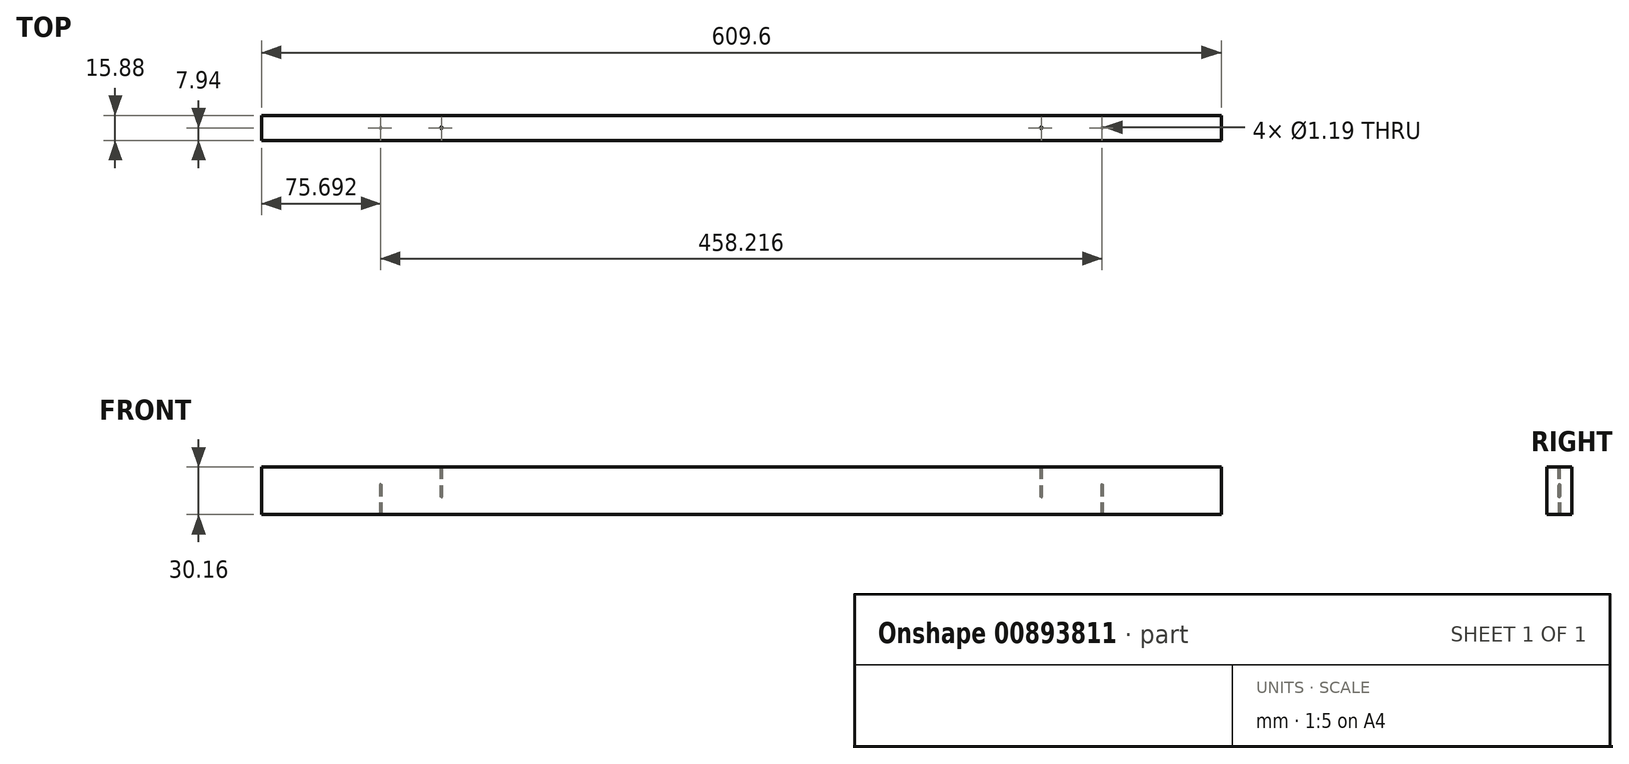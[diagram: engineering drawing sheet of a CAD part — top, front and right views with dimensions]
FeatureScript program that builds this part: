
annotation { "Feature Type Name" : "Feature", "Feature Type Description" : "" }
export const myFeature = defineFeature(function(context is Context, id is Id, definition is map)
    precondition{}
    {
        {
            var Q0;
            Q0=qCreatedBy(makeId("Top.planeOp"),FACE);
            var sketch = newSketch(context, id + "F0", { "sketchPlane" : qUnion([Q0])});
            skLineSegment(sketch, "E0.bottom", {"start": v(-304.8, 7.94) * mm, "end": v(304.8, 7.94) * mm});
            skLineSegment(sketch, "E0.top", {"start": v(-304.8, -7.94) * mm, "end": v(304.8, -7.94) * mm});
            skLineSegment(sketch, "E0.left", {"start": v(-304.8, 7.94) * mm, "end": v(-304.8, -7.94) * mm});
            skLineSegment(sketch, "E0.right", {"start": v(304.8, 7.94) * mm, "end": v(304.8, -7.94) * mm});
            skPoint(sketch, "E0.middle", {"position": v(0, 0) * mm});
            skSolve(sketch);
        }
        {
            var Q0;
            Q0=makeQuery(id+"F0.imprint","IMPRINT",FACE,{"disambiguationData":[TD([[makeQuery(id+"F0.imprint","IMPRINT",EDGE,{"derivedFrom":sQuery(id+"F0.wireOp",EDGE,"E0.bottom")}),-1.0]])]});
            extrude(context, id + "F1", {"entities" : qUnion([Q0]), "depth" : 30.16 * mm, "offsetDistance" : 25.4 * mm});
        }
        {
            var Q0;
            Q0=makeQuery(id+"F1.opExtrude","CAP_FACE",FACE,{"disambiguationData":[OSD([sQuery(id+"F0.wireOp",EDGE,"E0.bottom"),sQuery(id+"F0.wireOp",EDGE,"E0.top"),sQuery(id+"F0.wireOp",EDGE,"E0.left"),sQuery(id+"F0.wireOp",EDGE,"E0.right")])],"isStart":true});
            var sketch = newSketch(context, id + "F2", { "sketchPlane" : qUnion([Q0])});
            skPoint(sketch, "E1", {"position": v(229.1, 0) * mm});
            skPoint(sketch, "E2", {"position": v(-229.1, 0) * mm});
            skSolve(sketch);
        }
        {
            var Q0;
            Q0=sQuery(id+"F2.wireOp",VERTEX,"E1");
            var Q1;
            Q1=sQuery(id+"F2.wireOp",VERTEX,"E2");
            var Q2;
            Q2=makeQuery(id+"F1.opExtrude","SWEPT_BODY",BODY,{"disambiguationData":[OSD([sQuery(id+"F0.wireOp",EDGE,"E0.bottom"),sQuery(id+"F0.wireOp",EDGE,"E0.top"),sQuery(id+"F0.wireOp",EDGE,"E0.left"),sQuery(id+"F0.wireOp",EDGE,"E0.right")])]});
            hole(context, id + "F3", {"style" : HoleStyle.SIMPLE, "endStyle" : HoleEndStyle.BLIND, "holeDiameter" : 1.2 * mm, "majorDiameter" : 6.35 * mm, "holeDepth" : 19.05 * mm, "isTappedThrough" : true, "tappedDepth" : 12.7 * mm, "tapClearance" : 3, "locations" : qUnion([Q0, Q1]), "scope" : qUnion([Q2])});
        }
        {
            var Q0;
            Q0=makeQuery(id+"F1.opExtrude","CAP_FACE",FACE,{"disambiguationData":[OSD([sQuery(id+"F0.wireOp",EDGE,"E0.bottom"),sQuery(id+"F0.wireOp",EDGE,"E0.top"),sQuery(id+"F0.wireOp",EDGE,"E0.left"),sQuery(id+"F0.wireOp",EDGE,"E0.right")])],"isStart":false});
            var sketch = newSketch(context, id + "F4", { "sketchPlane" : qUnion([Q0])});
            skPoint(sketch, "E3", {"position": v(-190.5, 0) * mm});
            skPoint(sketch, "E4", {"position": v(190.5, 0) * mm});
            skSolve(sketch);
        }
        {
            var Q0;
            Q0=sQuery(id+"F4.wireOp",VERTEX,"E4");
            var Q1;
            Q1=sQuery(id+"F4.wireOp",VERTEX,"E3");
            var Q2;
            Q2=makeQuery(id+"F1.opExtrude","SWEPT_BODY",BODY,{"disambiguationData":[OSD([sQuery(id+"F0.wireOp",EDGE,"E0.bottom"),sQuery(id+"F0.wireOp",EDGE,"E0.top"),sQuery(id+"F0.wireOp",EDGE,"E0.left"),sQuery(id+"F0.wireOp",EDGE,"E0.right")])]});
            hole(context, id + "F5", {"style" : HoleStyle.SIMPLE, "endStyle" : HoleEndStyle.BLIND, "holeDiameter" : 1.2 * mm, "majorDiameter" : 6.35 * mm, "holeDepth" : 19.05 * mm, "isTappedThrough" : true, "tappedDepth" : 12.7 * mm, "tapClearance" : 3, "locations" : qUnion([Q0, Q1]), "scope" : qUnion([Q2])});
        }
    });
